# Revit family: FT116 Miura Desk USB - CE
name_source: partatom
category: Lighting Fixtures
units: mm (PartAtom-declared; Revit-internal decimal feet)

## family parameters
Always vertical = Yes
Cut with Voids When Loaded = No
Light Source = Yes
OmniClass Number = 23.80.70.00
OmniClass Title = Lighting
Part Type = Normal
Room Calculation Point = No
Round Connector Dimension = Use Diameter
Shared = No
Work Plane-Based = No

## types (2) — shared parameters
Color Filter = 16777215
Dimming Lamp Color Temperature Shift = <None>
Manufacturer URL - Europe and Rest of World = www.astrolighting.com
Manufacturer URL - North America = us.astrolighting.com
zero-valued in all types: Default Elevation

## per-type parameters (varying)
| type | ADA compliant | Dimmable | Dimming Method | Driver Included | Driver Required | Efficacy (lm/W) | Electrical Class | Lamp | Length of Cable Supplied | Light Source Fixed | Location / IP Rating | Main Finish | Main Material | Photometric Web File | Power (W) | Product CCT | Product CRI | Product Dimensions (MM) | Product Location | Product Name | Product SKU | Product Weight (KG) | Tilt Angle |
| 1444xxx Miura Desk USB | Not Applicable | No | Not Applicable | Integral | No | 49 | 2 | Integral LED | 2000mm | Adjustable | Indoor / IP20 | Matt Nickel | Zinc | 1444007_Miura Desk USB__Photometry_IES_Iss.01.ies | 7.5W | 2700K | 80 | 453x150x305 | Desk | Miura LED Desk USB | 1444007 | 2.142 | 90.00° |
| ETL |  |  |  |  |  |  |  |  |  |  |  |  |  | generic |  | 2700K / 3000K | 80 / 90 |  |  |  | 1234567 |  | 60.00° |

## geometry (parser evidence)
native form markers: Sweep x3
no freeform markers — native parametric forms only
